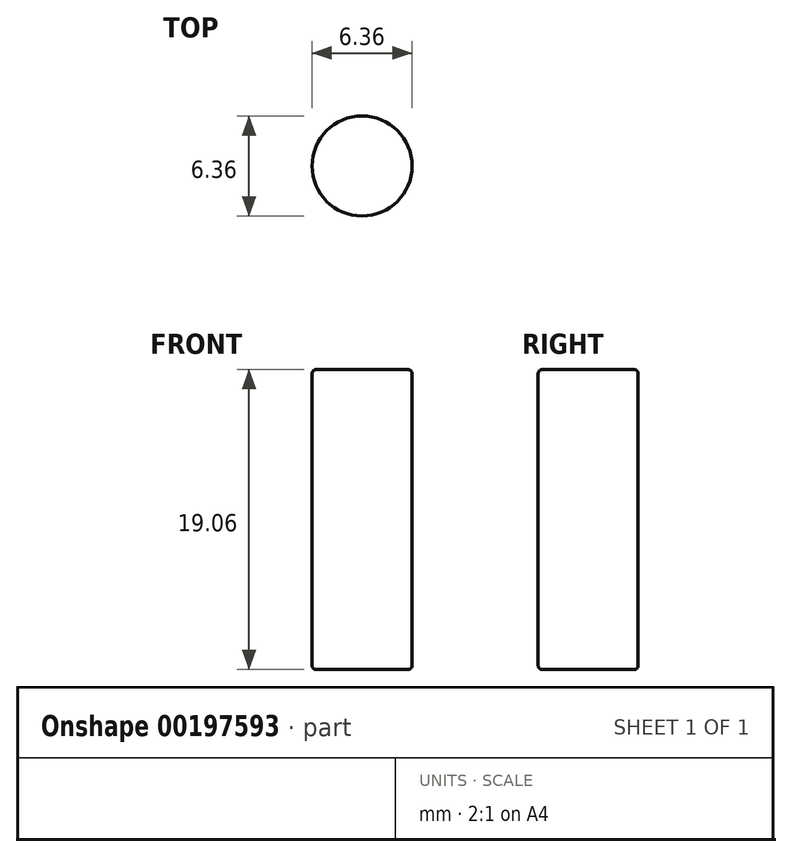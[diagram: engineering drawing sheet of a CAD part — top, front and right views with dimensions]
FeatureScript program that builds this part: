
annotation { "Feature Type Name" : "Feature", "Feature Type Description" : "" }
export const myFeature = defineFeature(function(context is Context, id is Id, definition is map)
    precondition{}
    {
        {
            var Q0;
            Q0=qCreatedBy(makeId("Top.planeOp"),FACE);
            var sketch = newSketch(context, id + "F0", { "sketchPlane" : qUnion([Q0])});
            skCircle(sketch, "E0", {"center": v(0, 0) * mm, "radius": 3.18 * mm});
            skSolve(sketch);
        }
        {
            var Q0;
            Q0=qSketchRegion(id+"F0",true);
            extrude(context, id + "F1", {"entities" : qUnion([Q0]), "endBound" : BoundingType.SYMMETRIC, "depth" : 19.05 * mm});
        }
        {
            var Q0;
            Q0=makeQuery(id+"F1.opExtrude","CAP_EDGE",EDGE,{"disambiguationData":[OSD([sQuery(id+"F0.wireOp",EDGE,"E0")])],"isStart":false});
            var Q1;
            Q1=makeQuery(id+"F1.opExtrude","CAP_EDGE",EDGE,{"disambiguationData":[OSD([sQuery(id+"F0.wireOp",EDGE,"E0")])],"isStart":true});
            fillet(context, id + "F2", {"entities" : qUnion([Q0, Q1]), "radius" : 0.25 * mm, "tangentPropagation" : true, "allowEdgeOverflow" : false});
        }
    });
